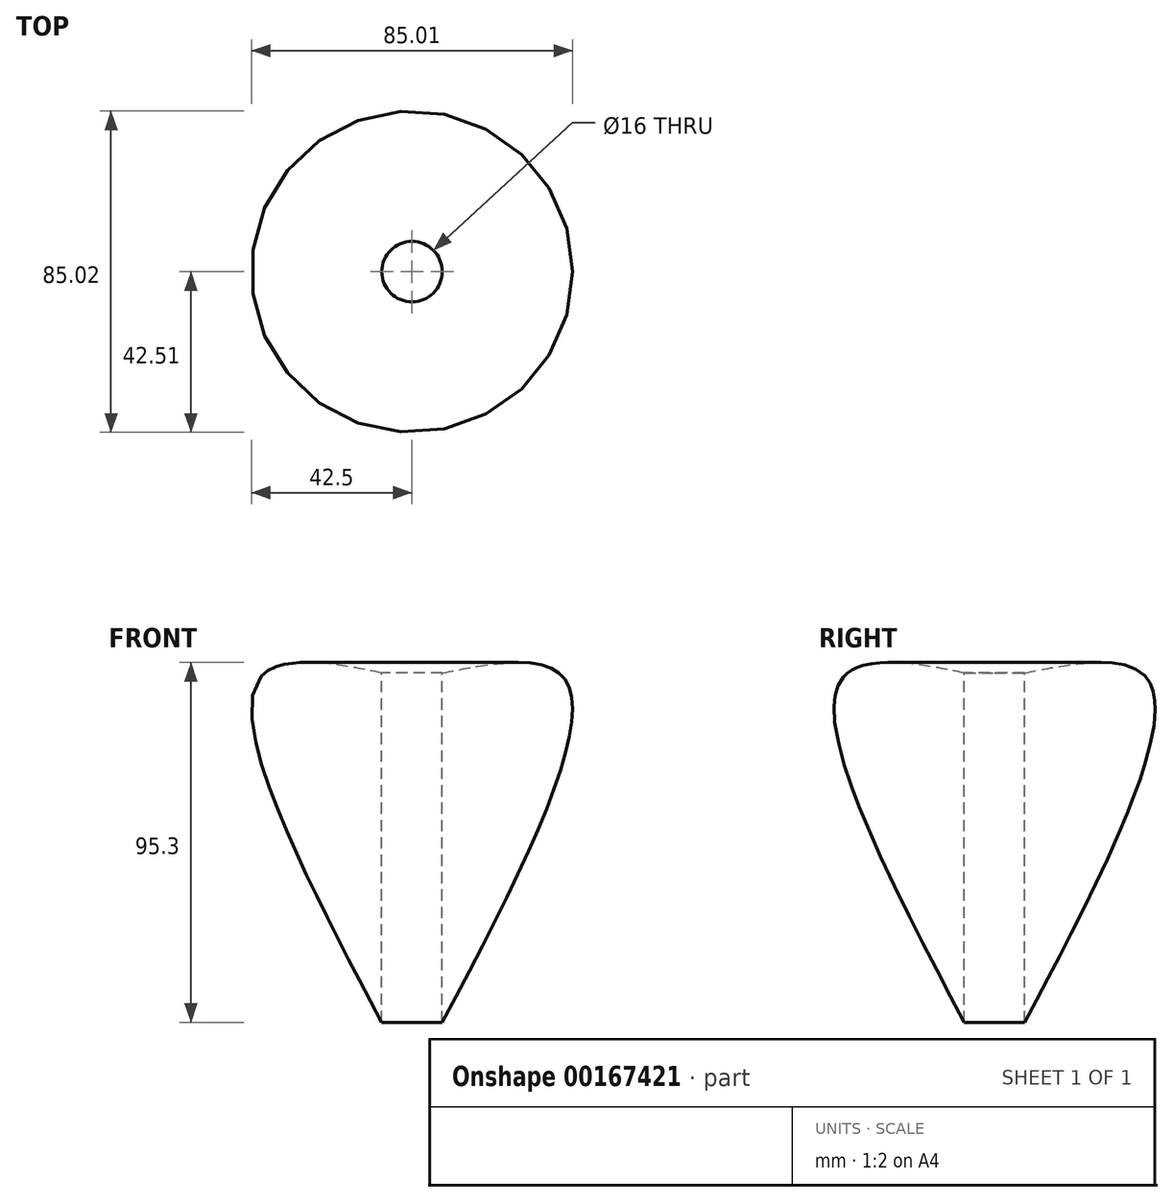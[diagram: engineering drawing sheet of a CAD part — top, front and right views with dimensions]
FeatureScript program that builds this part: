
annotation { "Feature Type Name" : "Feature", "Feature Type Description" : "" }
export const myFeature = defineFeature(function(context is Context, id is Id, definition is map)
    precondition{}
    {
        {
            var Q0;
            Q0=qCreatedBy(makeId("Right.planeOp"),FACE);
            var sketch = newSketch(context, id + "F0", { "sketchPlane" : qUnion([Q0])});
            skFitSpline(sketch, "E0", {"points": [v(0, 43.9) * mm, v(-40.6, 43.9) * mm, v(0, -61.76) * mm], "startDerivative": vector(-140.85, 31.64) * mm, "endDerivative": vector(119.1, -221.8) * mm});
            skLineSegment(sketch, "E1", {"start": v(0, 43.9) * mm, "end": v(0, -61.76) * mm});
            skSolve(sketch);
        }
        {
            var Q0;
            Q0=makeQuery(id+"F0.imprint","IMPRINT",FACE,{"disambiguationData":[TD([[makeQuery(id+"F0.imprint","IMPRINT",EDGE,{"derivedFrom":sQuery(id+"F0.wireOp",EDGE,"E0")}),1.0]])]});
            var Q1;
            Q1=sQuery(id+"F0.wireOp",EDGE,"E1");
            revolve(context, id + "F1", {"entities" : qUnion([Q0]), "axis" : qUnion([Q1]), "revolveType" : RevolveType.FULL});
        }
        {
            var Q0;
            Q0=qCreatedBy(makeId("Top.planeOp"),FACE);
            var sketch = newSketch(context, id + "F2", { "sketchPlane" : qUnion([Q0])});
            skCircle(sketch, "E2", {"center": v(0, 0) * mm, "radius": 8 * mm});
            skSolve(sketch);
        }
        {
            var Q0;
            Q0 = qSketchRegion(id + "F2", true);
            extrude(context, id + "F3", {"entities" : qUnion([Q0]), "operationType" : NewBodyOperationType.REMOVE, "endBound" : BoundingType.THROUGH_ALL, "oppositeDirection" : true, "depth" : 25 * mm, "hasSecondDirection" : true, "secondDirectionBound" : SecondDirectionBoundingType.THROUGH_ALL, "secondDirectionOppositeDirection" : false, "secondDirectionDepth" : 25 * mm});
        }
    });
